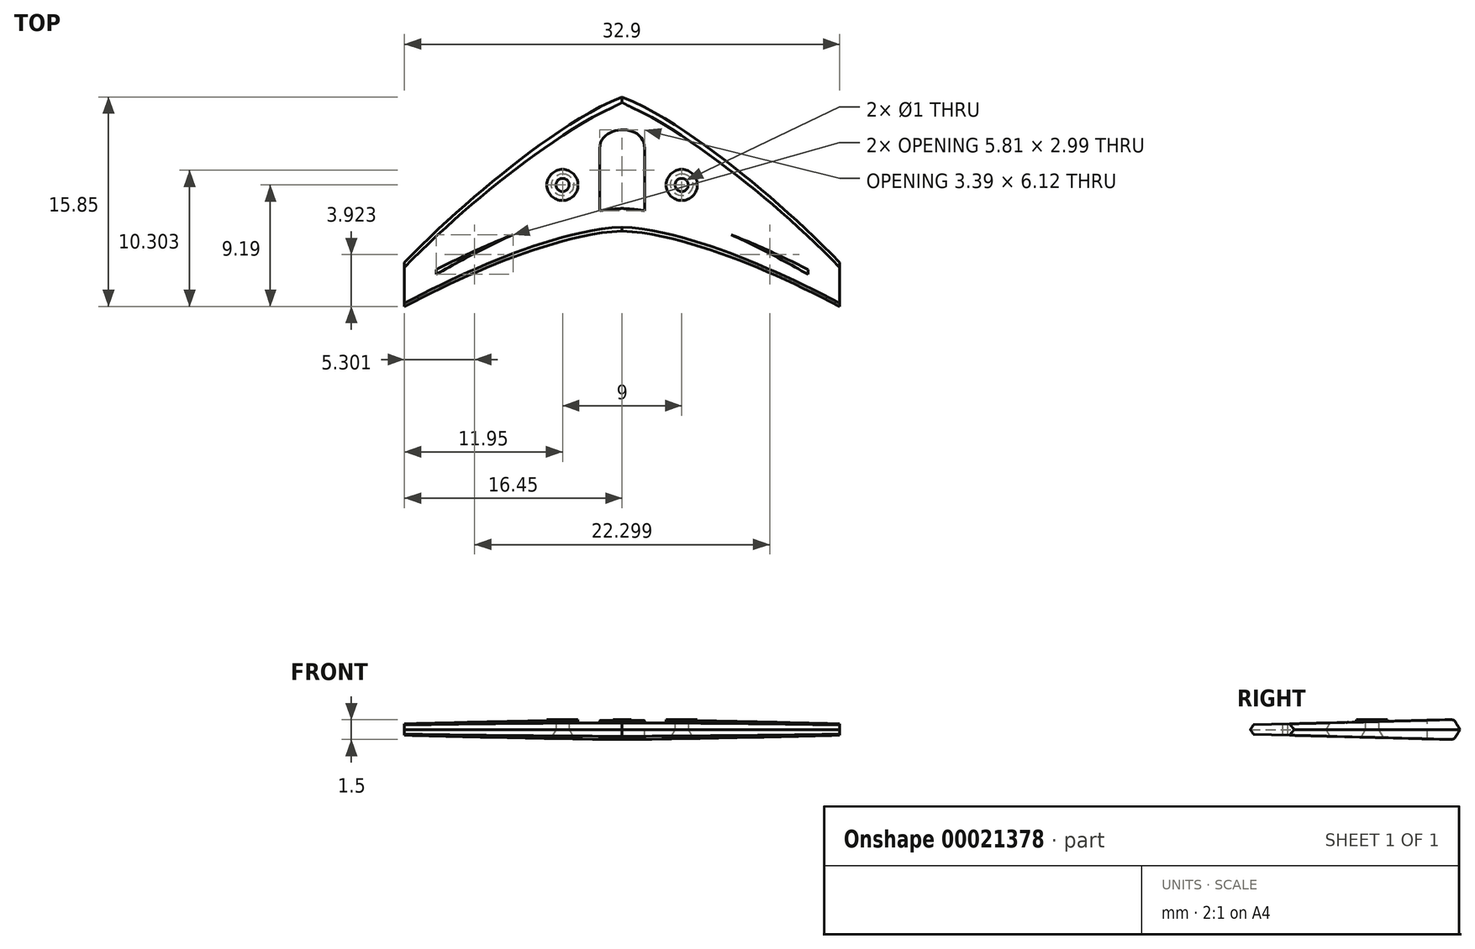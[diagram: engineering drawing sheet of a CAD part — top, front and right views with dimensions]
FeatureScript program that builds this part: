
annotation { "Feature Type Name" : "Feature", "Feature Type Description" : "" }
export const myFeature = defineFeature(function(context is Context, id is Id, definition is map)
    precondition{}
    {
        {
            var Q0;
            Q0=qCreatedBy(makeId("Top.planeOp"),FACE);
            var sketch = newSketch(context, id + "F0", { "sketchPlane" : qUnion([Q0])});
            skCircle(sketch, "E0", {"center": v(-4.5, 0) * mm, "radius": 0.5 * mm});
            skLineSegment(sketch, "E1", {"start": v(-16.5, 11.04) * mm, "end": v(-16.5, -11.29) * mm, "construction": true});
            skFitSpline(sketch, "E2", {"points": [v(-21.36, -11.9) * mm, v(0, 6.66) * mm], "startDerivative": vector(12.25, 19.51) * mm, "endDerivative": vector(17.06, 6.53) * mm});
            skCircle(sketch, "E3.MirrorC", {"center": v(4.5, 0) * mm, "radius": 0.5 * mm});
            skFitSpline(sketch, "E4.MirrorCS", {"points": [v(21.36, -11.9) * mm, v(0, 6.66) * mm], "startDerivative": vector(-12.25, 19.51) * mm, "endDerivative": vector(-17.06, 6.53) * mm});
            skFitSpline(sketch, "E5", {"points": [v(-21.36, -11.9) * mm, v(0, -3.48) * mm], "startDerivative": vector(18.81, 10.95) * mm, "endDerivative": vector(18.76, 1) * mm});
            skFitSpline(sketch, "E6.MirrorCS", {"points": [v(21.36, -11.9) * mm, v(0, -3.48) * mm], "startDerivative": vector(-18.81, 10.95) * mm, "endDerivative": vector(-18.76, 1) * mm});
            skLineSegment(sketch, "E7.MirrorCS", {"start": v(16.5, 11.04) * mm, "end": v(16.5, -11.29) * mm, "construction": true});
            skSolve(sketch);
        }
        {
            var Q0;
            Q0 = qSketchRegion(id + "F0", true);
            var Q1;
            Q1=sQuery(id+"F0.wireOp",EDGE,"E7.MirrorCS");
            extrude(context, id + "F1", {"entities" : qUnion([Q0]), "surfaceEntities" : qUnion([Q1]), "endBound" : BoundingType.SYMMETRIC, "depth" : 1.5 * mm, "hasDraft" : true, "draftAngle" : 30 * degree, "draftPullDirection" : true});
        }
        {
            var Q0;
            Q0=qCreatedBy(makeId("Top.planeOp"),FACE);
            var sketch = newSketch(context, id + "F2", { "sketchPlane" : qUnion([Q0])});
            skLineSegment(sketch, "E8.bottom", {"start": v(-16.45, 9.59) * mm, "end": v(-22.85, 9.59) * mm});
            skLineSegment(sketch, "E8.top", {"start": v(-16.45, -16.37) * mm, "end": v(-22.85, -16.37) * mm});
            skLineSegment(sketch, "E8.left", {"start": v(-16.45, 9.59) * mm, "end": v(-16.45, -16.37) * mm});
            skLineSegment(sketch, "E8.right", {"start": v(-22.85, 9.59) * mm, "end": v(-22.85, -16.37) * mm});
            skLineSegment(sketch, "E9.MirrorCS", {"start": v(16.45, 9.59) * mm, "end": v(16.45, -16.37) * mm});
            skLineSegment(sketch, "E10.MirrorCS", {"start": v(16.45, 9.59) * mm, "end": v(22.85, 9.59) * mm});
            skLineSegment(sketch, "E11.MirrorCS", {"start": v(22.85, 9.59) * mm, "end": v(22.85, -16.37) * mm});
            skLineSegment(sketch, "E12.MirrorCS", {"start": v(16.45, -16.37) * mm, "end": v(22.85, -16.37) * mm});
            skSolve(sketch);
        }
        {
            var Q0;
            Q0 = qSketchRegion(id + "F2", true);
            extrude(context, id + "F3", {"entities" : qUnion([Q0]), "operationType" : NewBodyOperationType.REMOVE, "endBound" : BoundingType.SYMMETRIC, "oppositeDirection" : true, "depth" : 25 * mm});
        }
        {
            var Q0;
            Q0=qCreatedBy(makeId("Top.planeOp"),FACE);
            var sketch = newSketch(context, id + "F4", { "sketchPlane" : qUnion([Q0])});
            skFitSpline(sketch, "E13.0", {"points": [v(22.87, -15.3) * mm, v(22.41, -14.57) * mm, v(21.24, -12.95) * mm, v(18.12, -9.38) * mm, v(14.2, -5.64) * mm, v(10.13, -2.3) * mm, v(7.17, -0.15) * mm, v(4.94, 1.26) * mm, v(3.41, 2.07) * mm, v(2.75, 2.35) * mm, v(2.46, 2.47) * mm]});
            skLineSegment(sketch, "E14.left", {"start": v(1.7, -1.99) * mm, "end": v(1.7, 2.78) * mm});
            skLineSegment(sketch, "E14.right", {"start": v(6.24, -2.94) * mm, "end": v(6.24, -0.5) * mm});
            skFitSpline(sketch, "E15.trimOffspring", {"points": [v(22.03, -10.95) * mm, v(20.46, -9.99) * mm, v(16.99, -7.96) * mm, v(11.26, -5.05) * mm, v(6.41, -3.12) * mm, v(2.67, -2.12) * mm, v(0.86, -1.84) * mm, v(-0.02, -1.78) * mm]});
            skLineSegment(sketch, "E16", {"start": v(14.05, -5.96) * mm, "end": v(14.05, -6.76) * mm});
            skPoint(sketch, "E17.visualSharp", {"position": v(14.05, -5.62) * mm});
            skArc(sketch, "E17.filletArc", {"start": v(14.05, -5.96) * mm, "mid": v(13.99, -5.65) * mm, "end": v(13.8, -5.4) * mm});
            skFitSpline(sketch, "E18", {"points": [v(6.24, -2.94) * mm, v(14.05, -6.76) * mm], "startDerivative": vector(7.7, -2.92) * mm, "endDerivative": vector(7.61, -4.34) * mm});
            skPoint(sketch, "E19.visualSharp", {"position": v(6.24, 0.42) * mm});
            skArc(sketch, "E19.filletArc", {"start": v(7.02, -0.1) * mm, "mid": v(6.5, -0.06) * mm, "end": v(6.24, -0.5) * mm});
            skFitSpline(sketch, "E20.MirrorCS", {"points": [v(-22.03, -10.95) * mm, v(-20.46, -9.99) * mm, v(-16.99, -7.96) * mm, v(-11.26, -5.05) * mm, v(-6.41, -3.12) * mm, v(-2.67, -2.12) * mm, v(-0.86, -1.84) * mm, v(0.02, -1.78) * mm]});
            skLineSegment(sketch, "E21.MirrorCS", {"start": v(-1.7, -1.99) * mm, "end": v(-1.7, 2.78) * mm});
            skLineSegment(sketch, "E22.MirrorCS", {"start": v(-6.24, -2.94) * mm, "end": v(-6.24, -0.5) * mm});
            skArc(sketch, "E23.MirrorCS", {"start": v(-7.02, -0.1) * mm, "mid": v(-6.5, -0.06) * mm, "end": v(-6.24, -0.5) * mm});
            skFitSpline(sketch, "E24.MirrorCS", {"points": [v(-6.24, -2.94) * mm, v(-14.05, -6.76) * mm], "startDerivative": vector(-7.7, -2.92) * mm, "endDerivative": vector(-7.61, -4.34) * mm});
            skFitSpline(sketch, "E25.MirrorCS", {"points": [v(-22.87, -15.3) * mm, v(-22.41, -14.57) * mm, v(-21.24, -12.95) * mm, v(-18.12, -9.38) * mm, v(-14.2, -5.64) * mm, v(-10.13, -2.3) * mm, v(-7.17, -0.15) * mm, v(-4.94, 1.26) * mm, v(-3.41, 2.07) * mm, v(-2.75, 2.35) * mm, v(-2.46, 2.47) * mm]});
            skLineSegment(sketch, "E26.MirrorCS", {"start": v(-14.05, -5.96) * mm, "end": v(-14.05, -6.76) * mm});
            skArc(sketch, "E27.MirrorCS", {"start": v(-14.05, -5.96) * mm, "mid": v(-13.99, -5.65) * mm, "end": v(-13.8, -5.4) * mm});
            skFitSpline(sketch, "E28.MirrorCS", {"points": [v(-22.87, -15.3) * mm, v(-22.41, -14.57) * mm, v(-21.24, -12.95) * mm, v(-18.12, -9.38) * mm, v(-14.2, -5.64) * mm, v(-10.13, -2.3) * mm, v(-7.17, -0.15) * mm, v(-4.94, 1.26) * mm, v(-3.41, 2.07) * mm, v(-2.75, 2.35) * mm, v(-2.46, 2.47) * mm]});
            skFitSpline(sketch, "E29", {"points": [v(-1.7, 2.78) * mm, v(1.7, 2.78) * mm], "startDerivative": vector(0.12, 5.47) * mm, "endDerivative": vector(-0.06, -5.64) * mm});
            skSolve(sketch);
        }
        {
            var Q0;
            Q0 = qSketchRegion(id + "F4", true);
            extrude(context, id + "F5", {"entities" : qUnion([Q0]), "operationType" : NewBodyOperationType.REMOVE, "endBound" : BoundingType.SYMMETRIC, "depth" : 2 * mm});
        }
        {
            var Q0;
            Q0=makeQuery(id+"F3.boolean.opBoolean","COPY",FACE,{"derivedFrom":makeQuery(id+"F3.opExtrude","SWEPT_FACE",FACE,{"disambiguationData":[OSD([sQuery(id+"F2.wireOp",EDGE,"E9.MirrorCS")])]})});
            var sketch = newSketch(context, id + "F6", { "sketchPlane" : qUnion([Q0])});
            skCircle(sketch, "E30", {"center": v(5.91, 0) * mm, "radius": 0.75 * mm});
            skLineSegment(sketch, "E31", {"start": v(-9.2, 0.35) * mm, "end": v(-9.2, -0.35) * mm});
            skLineSegment(sketch, "E32", {"start": v(-9.2, 0.35) * mm, "end": v(5.9, 0.75) * mm});
            skLineSegment(sketch, "E33", {"start": v(-9.2, -0.35) * mm, "end": v(5.9, -0.75) * mm});
            skSolve(sketch);
        }
        {
            var Q0;
            Q0 = qSketchRegion(id + "F6", true);
            extrude(context, id + "F7", {"entities" : qUnion([Q0]), "operationType" : NewBodyOperationType.INTERSECT, "oppositeDirection" : true, "depth" : 42.77 * mm});
        }
        {
            var Q0;
            Q0=qCreatedBy(makeId("Top.planeOp"),FACE);
            var sketch = newSketch(context, id + "F8", { "sketchPlane" : qUnion([Q0])});
            skCircle(sketch, "E34", {"center": v(-4.5, 0) * mm, "radius": 1.18 * mm});
            skCircle(sketch, "E35.MirrorC", {"center": v(4.5, 0) * mm, "radius": 1.18 * mm});
            skCircle(sketch, "E36.0", {"center": v(-4.5, 0) * mm, "radius": 0.5 * mm});
            skCircle(sketch, "E37.MirrorC", {"center": v(4.5, 0) * mm, "radius": 0.5 * mm});
            skSolve(sketch);
        }
        {
            var Q0;
            Q0 = qSketchRegion(id + "F8", true);
            extrude(context, id + "F9", {"entities" : qUnion([Q0]), "operationType" : NewBodyOperationType.ADD, "depth" : 0.75 * mm});
        }
    });
